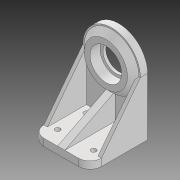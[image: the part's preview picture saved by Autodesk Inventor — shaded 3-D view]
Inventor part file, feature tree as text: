
AUTODESK INVENTOR PART (.ipt)
format: ipt  version: 2020 (Build 240168000, 168)  size: 390,144 bytes
history: native  units: mm
features: extrude x7, sketch x7, fillet x2, chamfer x1, mirror x1, projected_geometry x1
ambient origin geometry x8: Origin, YZ Plane, XZ Plane, XY Plane, X Axis, Y Axis, Z Axis, Center Point
bodies: Solid1 (feature_tree)
feature tree (19):
  extrude  "Extrusion1"  Depth=3.0mm
  extrude  "Extrusion2"  Depth=40.0mm
  fillet  "Fillet1"  Radius=38.0mm
  extrude  "Extrusion6"  Depth=40.0mm
  chamfer  "Chamfer1"  [1 undecoded]
  extrude  "Extrusion3"  Depth=20.0mm
  extrude  "Extrusion4"  Depth=25.0mm
  extrude  "Extrusion5"  TaperAngle=0.0deg  [1 undecoded]
  mirror  "Mirror1"
  fillet  "Fillet2"  Radius=2.5mm
  extrude  "Extrusion7"  Depth=5.0mm TaperAngle=0.0deg
  sketch  "Sketch1"  dims[d0=5.0mm d1=3.0mm]
  sketch  "Sketch2"  dims[d2=40.0mm d3=80.0mm d4=38.0mm d5=0.0mm]
  projected_geometry  "Projected Loop1"
  sketch  "Sketch3"  dims[d6=22.0mm d7=40.0mm d8=0.0mm d9=0.0mm]
  sketch  "Sketch4"  dims[d10=12.0mm d11=20.0mm]
  sketch  "Sketch5"  dims[d12=20.0mm d13=25.0mm]
  sketch  "Sketch6"  dims[d14=3.5mm d15=0.0mm d16=0.0mm d17=2.5mm d18=0.0mm]
  sketch  "Sketch7"  dims[d19=6.0mm d20=5.0mm d21=0.0mm d22=1.5mm d23=4.0mm d24=0.0mm d25=30.0mm d26=4.0mm d27=2.0mm d28=45.0deg d29=2.0mm d30=2.0mm d31=0.0mm]
note: 2 required parameter values undecoded (feature->parameter linkage not recoverable at this tier; creation-order binding heuristic only, values carry confidence <= 0.55)
